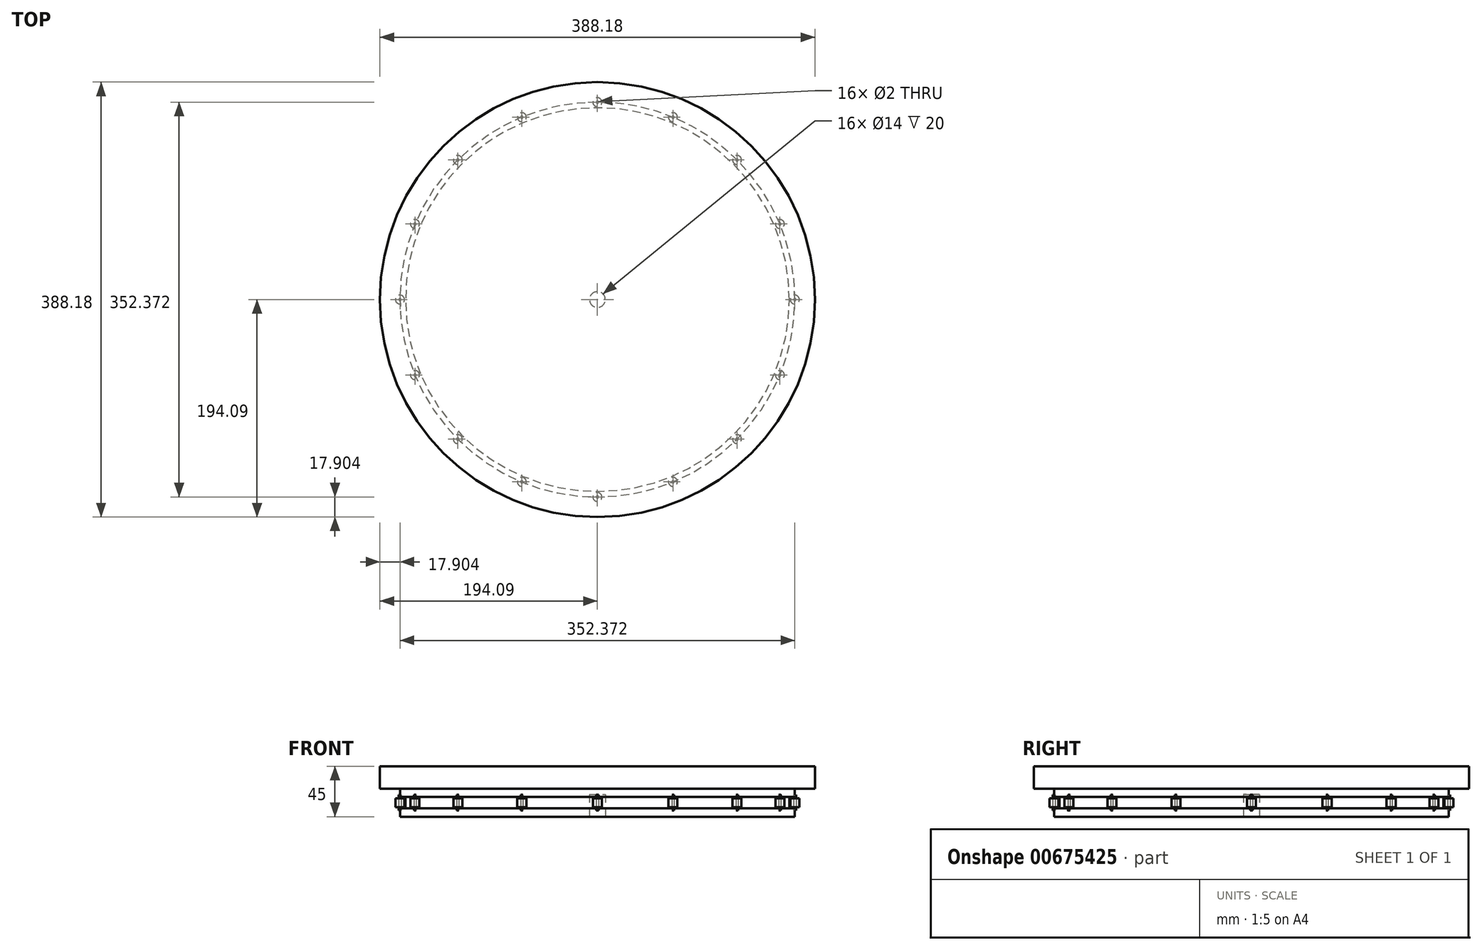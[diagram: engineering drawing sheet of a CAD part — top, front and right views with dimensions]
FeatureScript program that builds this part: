
annotation { "Feature Type Name" : "Feature", "Feature Type Description" : "" }
export const myFeature = defineFeature(function(context is Context, id is Id, definition is map)
    precondition{}
    {
        {
            var Q0;
            Q0=qCreatedBy(makeId("Top.planeOp"),FACE);
            var sketch = newSketch(context, id + "F0", { "sketchPlane" : qUnion([Q0])});
            skCircle(sketch, "E0", {"center": v(0, 0) * mm, "radius": 194.5 * mm});
            skCircle(sketch, "E1", {"center": v(0, 0) * mm, "radius": 177 * mm});
            skSolve(sketch);
        }
        {
            var Q0;
            Q0=qCreatedBy(makeId("Front.planeOp"),FACE);
            var sketch = newSketch(context, id + "F1", { "sketchPlane" : qUnion([Q0])});
            skLineSegment(sketch, "E2", {"start": v(194.09, 0) * mm, "end": v(194.09, -20) * mm});
            skLineSegment(sketch, "E3", {"start": v(194.09, -20) * mm, "end": v(176.19, -20) * mm});
            skLineSegment(sketch, "E4", {"start": v(176.19, -20) * mm, "end": v(176.19, -27.5) * mm});
            skLineSegment(sketch, "E5", {"start": v(176.19, -27.5) * mm, "end": v(171.19, -27.5) * mm});
            skLineSegment(sketch, "E6", {"start": v(171.19, -27.5) * mm, "end": v(171.19, -37.5) * mm});
            skLineSegment(sketch, "E7", {"start": v(171.19, -37.5) * mm, "end": v(176.19, -37.5) * mm});
            skLineSegment(sketch, "E8", {"start": v(176.19, -37.5) * mm, "end": v(176.19, -45) * mm});
            skLineSegment(sketch, "E9", {"start": v(176.19, -45) * mm, "end": v(0, -45) * mm});
            skLineSegment(sketch, "E10", {"start": v(0, -45) * mm, "end": v(0, 0) * mm});
            skLineSegment(sketch, "E11", {"start": v(0, 0) * mm, "end": v(194.09, 0) * mm});
            skLineSegment(sketch, "E12", {"start": v(176.19, -27.5) * mm, "end": v(176.19, -25.5) * mm});
            skLineSegment(sketch, "E13", {"start": v(176.19, -25.5) * mm, "end": v(177.19, -25.5) * mm});
            skLineSegment(sketch, "E14", {"start": v(177.19, -25.5) * mm, "end": v(177.19, -39.5) * mm});
            skLineSegment(sketch, "E15", {"start": v(177.19, -39.5) * mm, "end": v(176.19, -39.5) * mm});
            skLineSegment(sketch, "E16", {"start": v(176.19, -39.5) * mm, "end": v(176.19, -25.5) * mm});
            skLineSegment(sketch, "E17", {"start": v(176.19, -27.5) * mm, "end": v(176.19, -28.5) * mm});
            skLineSegment(sketch, "E18", {"start": v(176.19, -28.5) * mm, "end": v(180.19, -28.5) * mm});
            skLineSegment(sketch, "E19", {"start": v(180.19, -28.5) * mm, "end": v(180.19, -36.5) * mm});
            skLineSegment(sketch, "E20", {"start": v(180.19, -36.5) * mm, "end": v(176.19, -36.5) * mm});
            skSolve(sketch);
        }
        {
            var Q0;
            Q0=makeQuery(id+"F1.imprint","IMPRINT",FACE,{"disambiguationData":[TD([[makeQuery(id+"F1.imprint","IMPRINT",EDGE,{"derivedFrom":sQuery(id+"F1.wireOp",EDGE,"E2")}),-1.0]])]});
            var Q1;
            Q1=sQuery(id+"F0.wireOp",EDGE,"E1");
            revolve(context, id + "F2", {"surfaceOperationType" : NewSurfaceOperationType.NEW, "entities" : qUnion([Q0]), "axis" : qUnion([Q1]), "revolveType" : RevolveType.FULL});
        }
        {
            var Q0;
            {var subQ2=sQuery(id+"F1.wireOp",EDGE,"E13");Q0=makeQuery(id+"F1.imprint","IMPRINT",FACE,{"disambiguationData":[TD([[makeQuery(id+"F1.imprint","IMPRINT",EDGE,{"derivedFrom":subQ2}),-1.0]])]});}
            var Q1;
            {var subQ0=sQuery(id+"F1.wireOp",EDGE,"E18");var subQ1=sQuery(id+"F1.wireOp",EDGE,"E14");var subQ2=makeQuery(id+"F1.imprint","INTERSECT",VERTEX,{"derivedFrom":[subQ1,subQ0]});Q1=makeQuery(id+"F1.imprint","IMPRINT",FACE,{"disambiguationData":[TD([[makeQuery(id+"F1.imprint","IMPRINT",EDGE,{"disambiguationData":[TD([[subQ2,-1.0]])],"derivedFrom":subQ1}),-1.0]])]});}
            var Q2;
            {var subQ4=sQuery(id+"F1.wireOp",EDGE,"E15");Q2=makeQuery(id+"F1.imprint","IMPRINT",FACE,{"disambiguationData":[TD([[makeQuery(id+"F1.imprint","IMPRINT",EDGE,{"derivedFrom":subQ4}),-1.0]])]});}
            var Q3;
            Q3=sQuery(id+"F1.wireOp",EDGE,"E16");
            revolve(context, id + "F3", {"surfaceOperationType" : NewSurfaceOperationType.NEW, "entities" : qUnion([Q0, Q1, Q2]), "axis" : qUnion([Q3]), "revolveType" : RevolveType.FULL});
        }
        {
            var Q0;
            {var subQ5=sQuery(id+"F1.wireOp",EDGE,"E19");Q0=makeQuery(id+"F1.imprint","IMPRINT",FACE,{"disambiguationData":[TD([[makeQuery(id+"F1.imprint","IMPRINT",EDGE,{"derivedFrom":subQ5}),-1.0]])]});}
            var Q1;
            Q1=sQuery(id+"F1.wireOp",EDGE,"E16");
            revolve(context, id + "F4", {"surfaceOperationType" : NewSurfaceOperationType.NEW, "entities" : qUnion([Q0]), "axis" : qUnion([Q1]), "revolveType" : RevolveType.FULL});
        }
        {
            var Q0;
            Q0=makeQuery(id+"F4.opRevolve","SWEPT_BODY",BODY,{"disambiguationData":[OSD([sQuery(id+"F1.wireOp",EDGE,"E14"),sQuery(id+"F1.wireOp",EDGE,"E18"),sQuery(id+"F1.wireOp",EDGE,"E19"),sQuery(id+"F1.wireOp",EDGE,"E20")])]});
            var Q1;
            Q1=makeQuery(id+"F3.opRevolve","SWEPT_BODY",BODY,{"disambiguationData":[OSD([sQuery(id+"F1.wireOp",EDGE,"E13"),sQuery(id+"F1.wireOp",EDGE,"E14"),sQuery(id+"F1.wireOp",EDGE,"E15"),sQuery(id+"F1.wireOp",EDGE,"E16"),sQuery(id+"F1.wireOp",EDGE,"E17")])]});
            var Q2;
            Q2=makeQuery(id+"F2.opRevolve","SWEPT_BODY",BODY,{"disambiguationData":[OSD([sQuery(id+"F1.wireOp",EDGE,"E2"),sQuery(id+"F1.wireOp",EDGE,"E3"),sQuery(id+"F1.wireOp",EDGE,"E4"),sQuery(id+"F1.wireOp",EDGE,"E5"),sQuery(id+"F1.wireOp",EDGE,"E6"),sQuery(id+"F1.wireOp",EDGE,"E7"),sQuery(id+"F1.wireOp",EDGE,"E8"),sQuery(id+"F1.wireOp",EDGE,"E9"),sQuery(id+"F1.wireOp",EDGE,"E10"),sQuery(id+"F1.wireOp",EDGE,"E11"),sQuery(id+"F1.wireOp",EDGE,"E16")])]});
            var Q3;
            Q3=sQuery(id+"F1.wireOp",EDGE,"E10");
            circularPattern(context, id + "F5", {"entities" : qUnion([Q0, Q1, Q2]), "axis" : qUnion([Q3]), "angle" : 360 * degree, "instanceCount" : 16, "equalSpace" : true});
        }
        {
            var Q0;
            Q0=makeQuery(id+"F2.opRevolve","SWEPT_FACE",FACE,{"disambiguationData":[OSD([sQuery(id+"F1.wireOp",EDGE,"E9")])]});
            var sketch = newSketch(context, id + "F6", { "sketchPlane" : qUnion([Q0])});
            skCircle(sketch, "E21", {"center": v(0, 0) * mm, "radius": 7 * mm});
            skSolve(sketch);
        }
        {
            var Q0;
            Q0=makeQuery(id+"F6.imprint","IMPRINT",FACE,{"disambiguationData":[TD([[makeQuery(id+"F6.imprint","IMPRINT",EDGE,{"derivedFrom":sQuery(id+"F6.wireOp",EDGE,"E21")}),1.0]])]});
            extrude(context, id + "F7", {"entities" : qUnion([Q0]), "operationType" : NewBodyOperationType.REMOVE, "oppositeDirection" : true, "depth" : 20 * mm, "offsetDistance" : 25 * mm});
        }
    });
